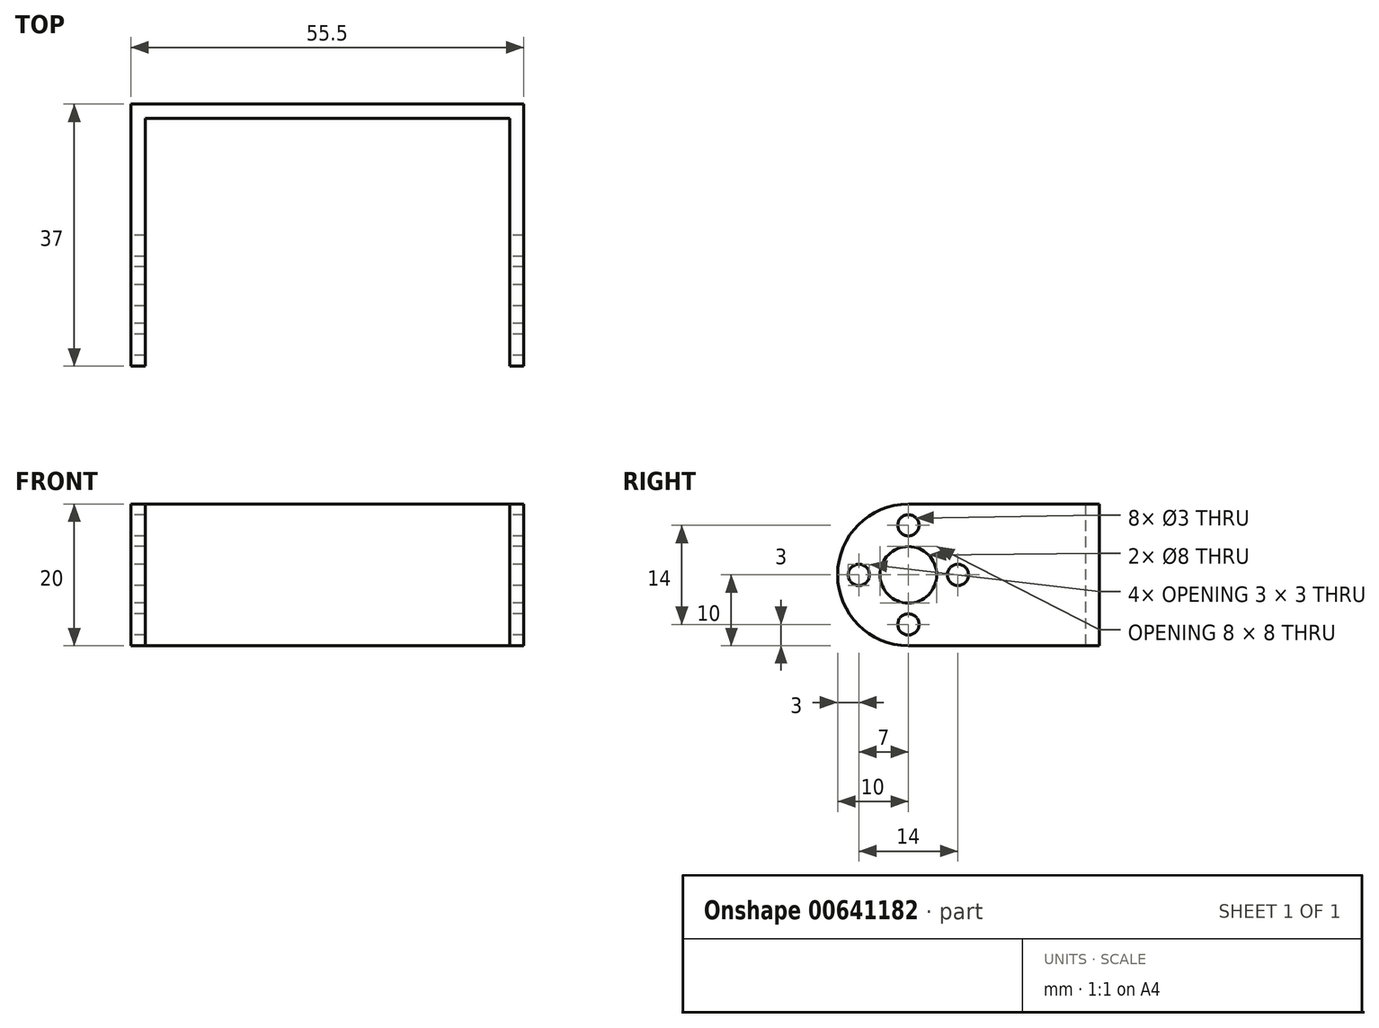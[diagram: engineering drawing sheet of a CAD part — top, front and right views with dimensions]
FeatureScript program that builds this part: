
annotation { "Feature Type Name" : "Feature", "Feature Type Description" : "" }
export const myFeature = defineFeature(function(context is Context, id is Id, definition is map)
    precondition{}
    {
        {
            var Q0;
            Q0=qCreatedBy(makeId("Top.planeOp"),FACE);
            var sketch = newSketch(context, id + "F0", { "sketchPlane" : qUnion([Q0])});
            skLineSegment(sketch, "E0", {"start": v(-27.75, 0) * mm, "end": v(-27.75, 37) * mm});
            skLineSegment(sketch, "E1", {"start": v(-27.75, 37) * mm, "end": v(27.75, 37) * mm});
            skLineSegment(sketch, "E2", {"start": v(27.75, 37) * mm, "end": v(27.75, 0) * mm});
            skLineSegment(sketch, "E3", {"start": v(27.75, 0) * mm, "end": v(25.75, 0) * mm});
            skLineSegment(sketch, "E4", {"start": v(25.75, 0) * mm, "end": v(25.75, 35) * mm});
            skLineSegment(sketch, "E5", {"start": v(25.75, 35) * mm, "end": v(-25.75, 35) * mm});
            skLineSegment(sketch, "E6", {"start": v(-25.75, 35) * mm, "end": v(-25.75, 0) * mm});
            skLineSegment(sketch, "E7", {"start": v(-25.75, 0) * mm, "end": v(-27.75, 0) * mm});
            skLineSegment(sketch, "E8", {"start": v(0, 41.28) * mm, "end": v(0, -18.39) * mm, "construction": true});
            skSolve(sketch);
        }
        {
            var Q0;
            Q0=makeQuery(id+"F0.imprint","IMPRINT",FACE,{"disambiguationData":[TD([[makeQuery(id+"F0.imprint","IMPRINT",EDGE,{"derivedFrom":sQuery(id+"F0.wireOp",EDGE,"E0")}),-1.0]])]});
            extrude(context, id + "F1", {"entities" : qUnion([Q0]), "depth" : 20 * mm, "offsetDistance" : 25 * mm});
        }
        {
            var Q0;
            Q0=makeQuery(id+"F1.opExtrude","CAP_EDGE",EDGE,{"disambiguationData":[OSD([sQuery(id+"F0.wireOp",EDGE,"E7")])],"isStart":true});
            var Q1;
            Q1=makeQuery(id+"F1.opExtrude","CAP_EDGE",EDGE,{"disambiguationData":[OSD([sQuery(id+"F0.wireOp",EDGE,"E7")])],"isStart":false});
            var Q2;
            Q2=makeQuery(id+"F1.opExtrude","CAP_EDGE",EDGE,{"disambiguationData":[OSD([sQuery(id+"F0.wireOp",EDGE,"E3")])],"isStart":true});
            var Q3;
            Q3=makeQuery(id+"F1.opExtrude","CAP_EDGE",EDGE,{"disambiguationData":[OSD([sQuery(id+"F0.wireOp",EDGE,"E3")])],"isStart":false});
            fillet(context, id + "F2", {"entities" : qUnion([Q0, Q1, Q2, Q3]), "radius" : 10 * mm, "tangentPropagation" : true, "allowEdgeOverflow" : false});
        }
        {
            var Q0;
            Q0=makeQuery(id+"F1.opExtrude","SWEPT_FACE",FACE,{"disambiguationData":[OSD([sQuery(id+"F0.wireOp",EDGE,"E0")])]});
            var sketch = newSketch(context, id + "F3", { "sketchPlane" : qUnion([Q0])});
            skLineSegment(sketch, "E9", {"start": v(-10, 20) * mm, "end": v(-10, 0) * mm, "construction": true});
            skLineSegment(sketch, "E10", {"start": v(-37, 10) * mm, "end": v(0, 10) * mm, "construction": true});
            skCircle(sketch, "E11", {"center": v(-10, 10) * mm, "radius": 4 * mm});
            skCircle(sketch, "E12", {"center": v(-10, 3) * mm, "radius": 1.5 * mm});
            skCircle(sketch, "E13.MirrorC", {"center": v(-10, 17) * mm, "radius": 1.5 * mm});
            skCircle(sketch, "E14", {"center": v(-3, 10) * mm, "radius": 1.5 * mm});
            skCircle(sketch, "E15.MirrorC", {"center": v(-17, 10) * mm, "radius": 1.5 * mm});
            skSolve(sketch);
        }
        {
            var Q0;
            Q0 = qSketchRegion(id + "F3", true);
            extrude(context, id + "F4", {"entities" : qUnion([Q0]), "operationType" : NewBodyOperationType.REMOVE, "endBound" : BoundingType.THROUGH_ALL, "oppositeDirection" : true, "depth" : 25 * mm, "offsetDistance" : 25 * mm});
        }
    });
